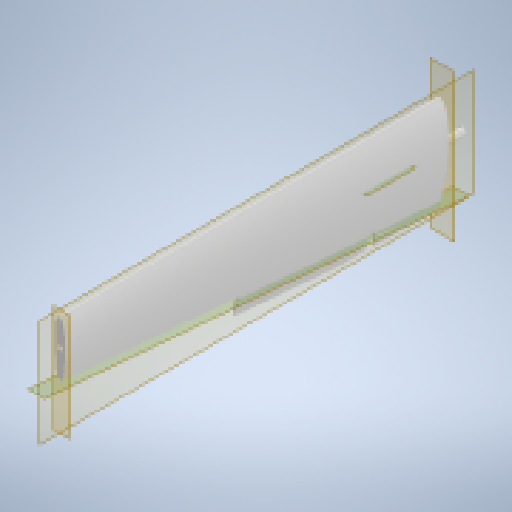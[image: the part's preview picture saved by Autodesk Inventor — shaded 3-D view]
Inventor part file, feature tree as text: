
AUTODESK INVENTOR PART (.ipt)
format: ipt  version: 2025 (Build 290162000, 162)  size: 500,736 bytes
history: native  units: in
note: dims shown in document units (in); Inventor stores cm internally (conversion verified against a paired STEP export)
features: sketch x16, extrude x13, plane x7, projected_geometry x7, other x6, reference x2, loft x1, mirror x1, sweep x1
ambient origin geometry x8: Origin, YZ Plane, XZ Plane, XY Plane, X Axis, Y Axis, Z Axis, Center Point
bodies: Solid1 (feature_tree)
feature tree (54):
  plane  "Work Plane1"
  extrude  "Extrusion1"  Depth=3.0in TaperAngle=0.0deg
  extrude  "Extrusion3"  Depth=7.382in
  plane  "Work Plane2"
  extrude  "Extrusion4"  TaperAngle=0.0deg  [1 undecoded]
  plane  "Work Plane3"
  plane  "Work Plane6"
  loft  "Loft2"
  plane  "Work Plane7"
  extrude  "Extrusion6"  Depth=9.5in
  extrude  "Extrusion7"  Depth=24.0in
  extrude  "Extrusion8"  Depth=1.75in TaperAngle=0.0deg
  extrude  "Extrusion9"  Depth=0.4724in
  extrude  "Extrusion10"  Depth=0.2559in TaperAngle=0.0deg
  extrude  "Extrusion11"  Depth=2.0in TaperAngle=0.0deg
  plane  "Work Plane8"
  mirror  "Mirror1"
  extrude  "Extrusion12"  Depth=0.4724in
  extrude  "Extrusion13"  Depth=0.8268in TaperAngle=0.0deg
  extrude  "Extrusion14"  Depth=0.0984in
  extrude  "Extrusion15"  Depth=0.0787in
  sketch  "Sketch18"  dims[d51=0.0787in d52=0.0787in]
  sweep  "Sweep1"
  sketch  "Sketch1"  dims[d0=13.7795in d1=0.0in d4=3.0in d5=0.0in]
  reference  "Reference1"
  sketch  "Sketch3"  dims[d6=37.4016in d7=7.382in]
  reference  "Reference3"
  sketch  "Sketch4"  dims[d8=0.1in d9=0.0in d15=0.0in]
  projected_geometry  "Projected Loop2"
  plane  "Work Plane5"
  other  "Edges3"
  other  "Edges4"
  sketch  "Sketch8"  dims[d16=0.0in d17=90.0deg d18=0.0in d19=90.0deg]
  sketch  "Sketch9"  dims[d24=1.125in d25=9.5in]
  sketch  "Sketch10"  dims[d26=0.0in d27=0.0in d28=24.0in]
  sketch  "Sketch11"  dims[d29=2.5in d30=1.75in d31=0.0in]
  sketch  "Sketch12"  dims[d32=0.4724in d33=1.2205in]
  projected_geometry  "Projected Loop4"
  sketch  "Sketch13"  dims[d34=0.125in d35=0.2559in d36=0.0in]
  projected_geometry  "Projected Loop5"
  sketch  "Sketch14"  dims[d37=2.0in d38=0.2559in d39=0.0in]
  sketch  "Sketch15"  dims[d40=0.4724in d41=0.9055in]
  projected_geometry  "Projected Loop6"
  sketch  "Sketch16"  dims[d44=0.0in d45=0.8268in d46=0.0in]
  sketch  "Sketch17"  dims[d49=0.0984in d50=0.0984in]
  projected_geometry  "Projected Loop7"
  sketch  "Sketch19"  dims[d53=0.25in d54=0.0in d55=0.5in]
  projected_geometry  "Projected Loop8"
  projected_geometry  "Projected Loop9"
  sketch  "Sketch20"  dims[d56=0.5in d57=0.5in d58=0.0in d59=1.06in d60=45.0in d61=0.0in d62=3.0in d63=-0.0069in d64=0.0in d65=2.0in d66=0.0in d67=0.0in d68=0.0in d20=0.5in d21=0.0344in d22=0.5in d23=0.0344in]
  other  "Wing.iam"
  other  "WingBox:1"
  other  "UAV_Assembly.iam"
  other  "Boom:1"
note: 1 required parameter value undecoded (feature->parameter linkage not recoverable at this tier; creation-order binding heuristic only, values carry confidence <= 0.55)
